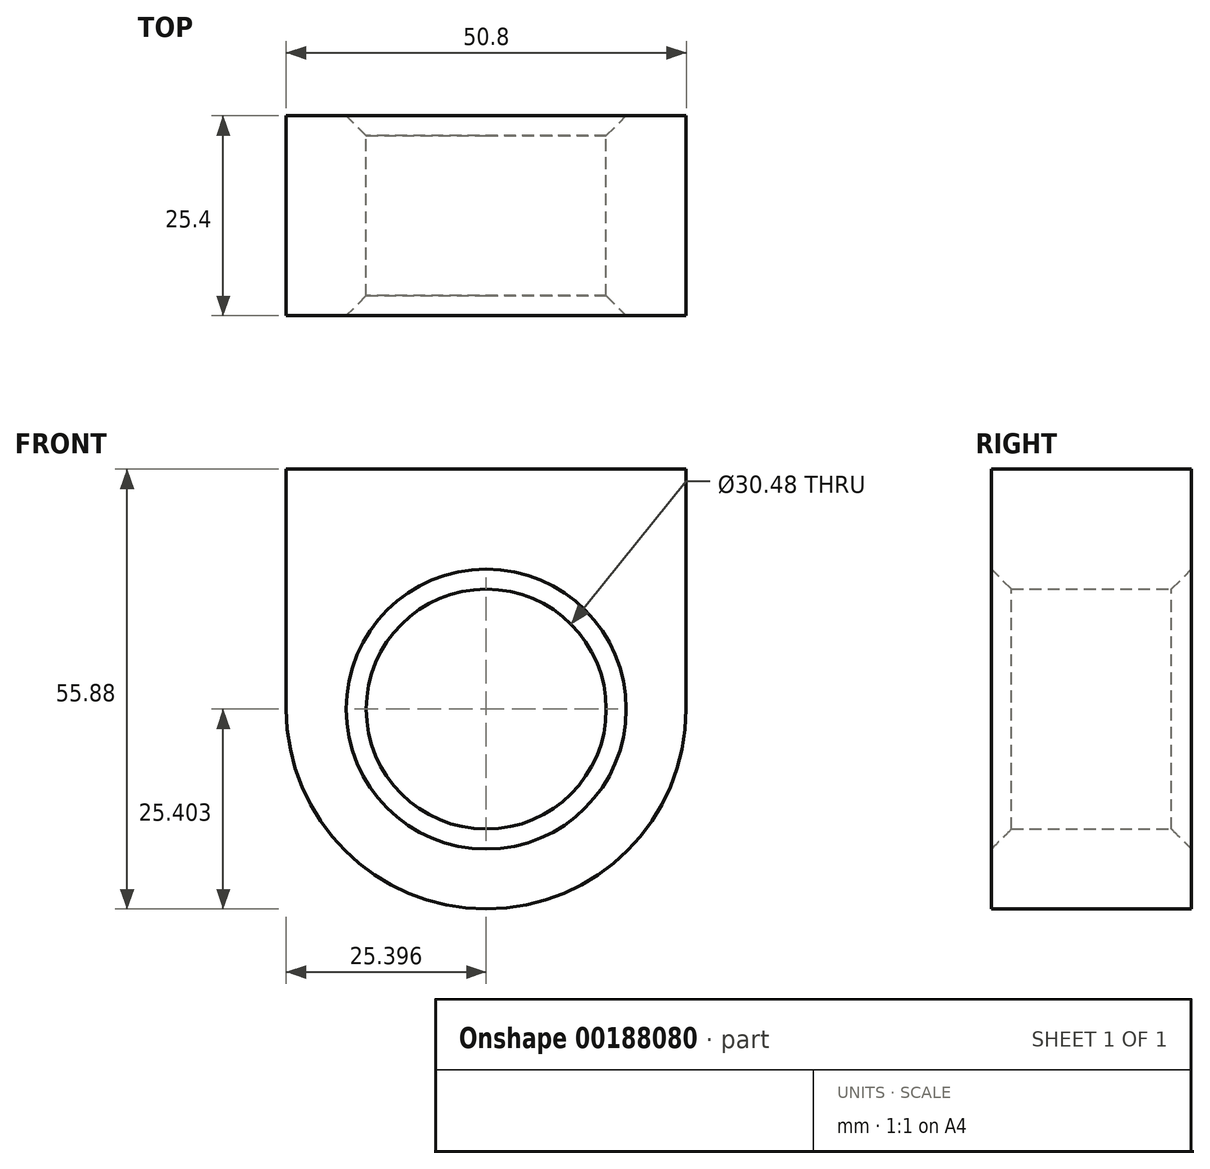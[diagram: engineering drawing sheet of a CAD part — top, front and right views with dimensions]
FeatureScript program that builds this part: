
annotation { "Feature Type Name" : "Feature", "Feature Type Description" : "" }
export const myFeature = defineFeature(function(context is Context, id is Id, definition is map)
    precondition{}
    {
        {
            var Q0;
            Q0=qCreatedBy(makeId("Front.planeOp"),FACE);
            var sketch = newSketch(context, id + "F0", { "sketchPlane" : qUnion([Q0])});
            skLineSegment(sketch, "E0.bottom", {"start": v(-24.71, 1.74) * mm, "end": v(26.09, 1.74) * mm});
            skLineSegment(sketch, "E0.left", {"start": v(-24.71, 1.74) * mm, "end": v(-24.71, -28.74) * mm});
            skLineSegment(sketch, "E0.right", {"start": v(26.09, 1.74) * mm, "end": v(26.09, -28.74) * mm});
            skArc(sketch, "E1", {"start": v(-24.71, -28.74) * mm, "mid": v(0.69, -54.14) * mm, "end": v(26.09, -28.74) * mm});
            skCircle(sketch, "E2", {"center": v(0.69, -28.74) * mm, "radius": 15.24 * mm});
            skSolve(sketch);
        }
        {
            var Q0;
            Q0=makeQuery(id+"F0.imprint","IMPRINT",FACE,{"disambiguationData":[TD([[makeQuery(id+"F0.imprint","IMPRINT",EDGE,{"derivedFrom":sQuery(id+"F0.wireOp",EDGE,"E0.bottom")}),-1.0]])]});
            extrude(context, id + "F1", {"entities" : qUnion([Q0]), "depth" : 25.4 * mm});
        }
        {
            var Q0;
            Q0=makeQuery(id+"F1.opExtrude","CAP_EDGE",EDGE,{"disambiguationData":[OSD([sQuery(id+"F0.wireOp",EDGE,"E2")])],"isStart":false});
            var Q1;
            Q1=makeQuery(id+"F1.opExtrude","CAP_EDGE",EDGE,{"disambiguationData":[OSD([sQuery(id+"F0.wireOp",EDGE,"E2")])],"isStart":true});
            chamfer(context, id + "F2", {"entities" : qUnion([Q0, Q1]), "width" : 2.54 * mm, "tangentPropagation" : true});
        }
    });
